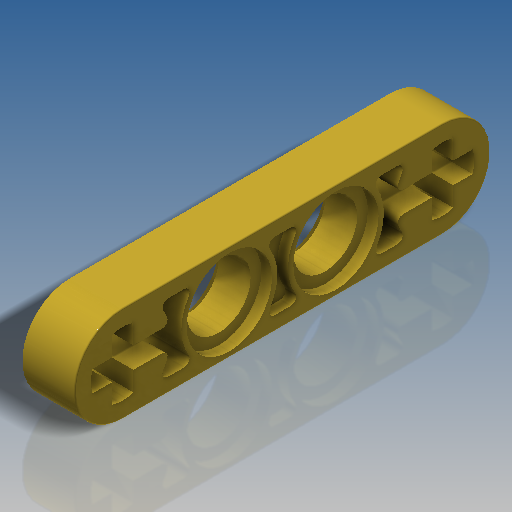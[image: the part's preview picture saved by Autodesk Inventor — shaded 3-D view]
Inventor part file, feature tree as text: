
AUTODESK INVENTOR PART (.ipt)
format: ipt  version: 2018.3 (Build 223284000, 284)  size: 342,016 bytes
history: native  units: mm
features: extrude x3, sketch x2, mirror x1, fillet x1
ambient origin geometry x8: Origin, YZ Plane, XZ Plane, XY Plane, X Axis, Y Axis, Z Axis, Center Point
bodies: Solid1 (feature_tree)
feature tree (7):
  extrude  "Extrusion4"  Depth=7.2mm
  sketch  "Sketch11"  dims[d53=1.6mm d56=0.1mm d58=24.0mm d59=6.4mm d60=4.8mm d61=6.4mm d62=0.8mm d63=0.0mm d64=45.0deg d65=0.8mm d66=0.0mm d67=0.4mm]
  extrude  "Extrusion16"  Depth=0.1mm
  extrude  "Extrusion17"  Depth=24.0mm
  mirror  "Mirror3"
  fillet  "Fillet1"  Radius=6.4mm
  sketch  "Sketch3"  dims[d15=4.0mm d16=0.0mm d47=4.8mm d49=7.2mm]
